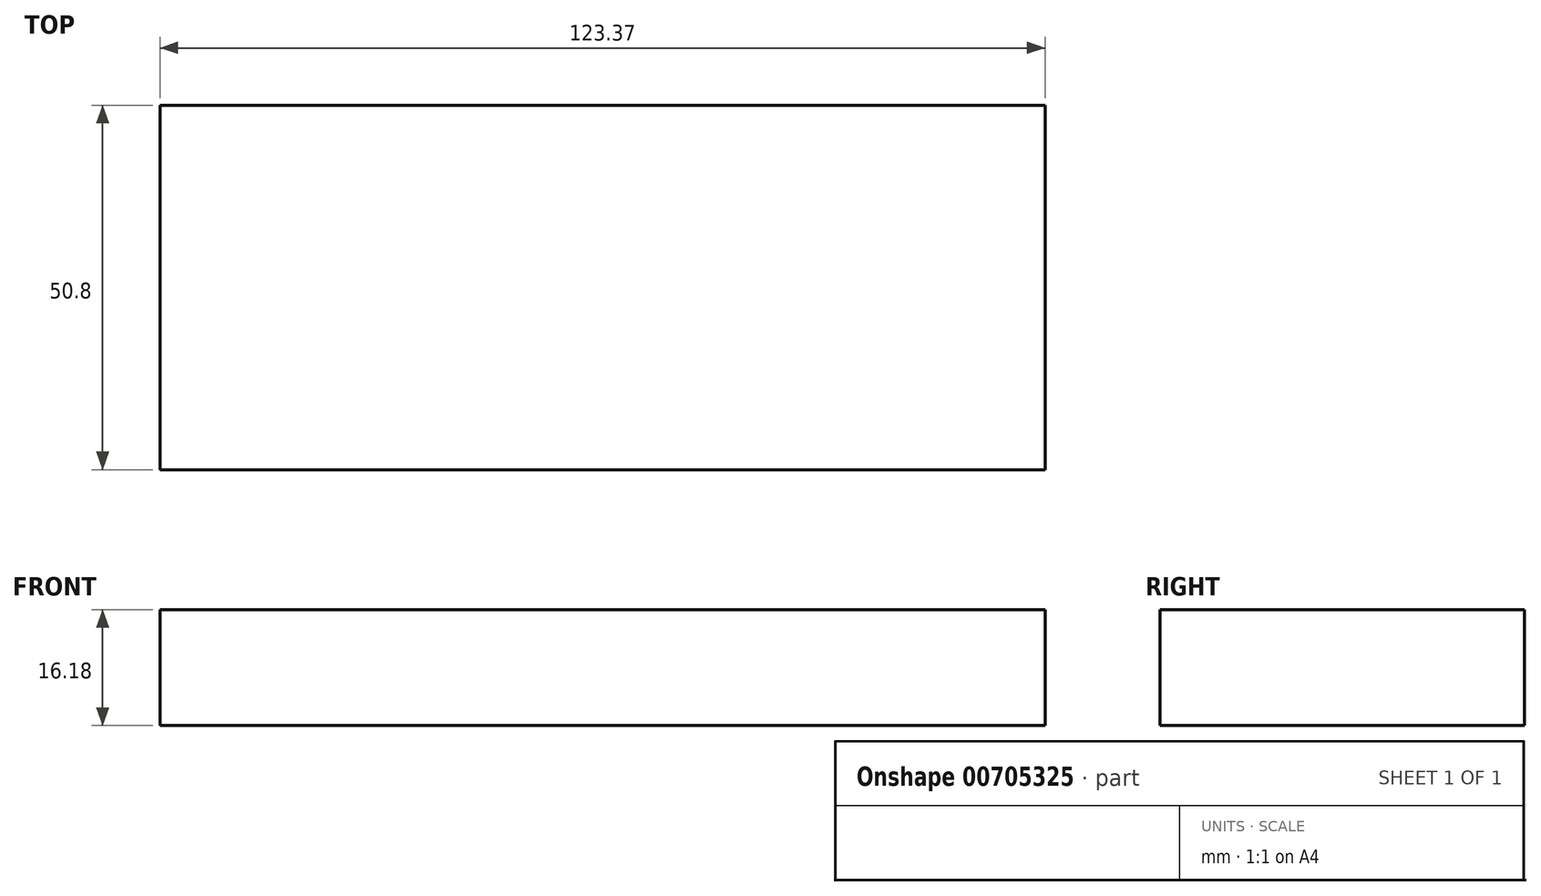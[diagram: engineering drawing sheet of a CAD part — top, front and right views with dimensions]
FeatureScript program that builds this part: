
annotation { "Feature Type Name" : "Feature", "Feature Type Description" : "" }
export const myFeature = defineFeature(function(context is Context, id is Id, definition is map)
    precondition{}
    {
        {
            var Q0;
            Q0=qCreatedBy(makeId("Front.planeOp"),FACE);
            var sketch = newSketch(context, id + "F0", { "sketchPlane" : qUnion([Q0])});
            skLineSegment(sketch, "E0.bottom", {"start": v(-64.9, 49.62) * mm, "end": v(58.48, 49.62) * mm});
            skLineSegment(sketch, "E0.top", {"start": v(-64.9, 33.44) * mm, "end": v(58.48, 33.44) * mm});
            skLineSegment(sketch, "E0.left", {"start": v(-64.9, 49.62) * mm, "end": v(-64.9, 33.44) * mm});
            skLineSegment(sketch, "E0.right", {"start": v(58.48, 49.62) * mm, "end": v(58.48, 33.44) * mm});
            skLineSegment(sketch, "E1.bottom", {"start": v(-125.05, 12.98) * mm, "end": v(-124.14, 12.98) * mm});
            skLineSegment(sketch, "E1.top", {"start": v(-125.05, 10.23) * mm, "end": v(-124.14, 10.23) * mm});
            skLineSegment(sketch, "E1.left", {"start": v(-125.05, 12.98) * mm, "end": v(-125.05, 10.23) * mm});
            skLineSegment(sketch, "E1.right", {"start": v(-124.14, 12.98) * mm, "end": v(-124.14, 10.23) * mm});
            skSolve(sketch);
        }
        {
            var Q0;
            Q0=makeQuery(id+"F0.imprint","IMPRINT",FACE,{"disambiguationData":[TD([[makeQuery(id+"F0.imprint","IMPRINT",EDGE,{"derivedFrom":sQuery(id+"F0.wireOp",EDGE,"E0.bottom")}),-1.0]])]});
            extrude(context, id + "F1", {"entities" : qUnion([Q0]), "depth" : 25.4 * mm, "offsetDistance" : 25.4 * mm});
        }
        {
            var Q0;
            Q0=makeQuery(id+"F1.opExtrude","CAP_FACE",FACE,{"disambiguationData":[OSD([sQuery(id+"F0.wireOp",EDGE,"E0.bottom"),sQuery(id+"F0.wireOp",EDGE,"E0.top"),sQuery(id+"F0.wireOp",EDGE,"E0.left"),sQuery(id+"F0.wireOp",EDGE,"E0.right")])],"isStart":false});
            extrude(context, id + "F2", {"entities" : qUnion([Q0]), "operationType" : NewBodyOperationType.ADD, "depth" : 25.4 * mm, "offsetDistance" : 25.4 * mm});
        }
    });
